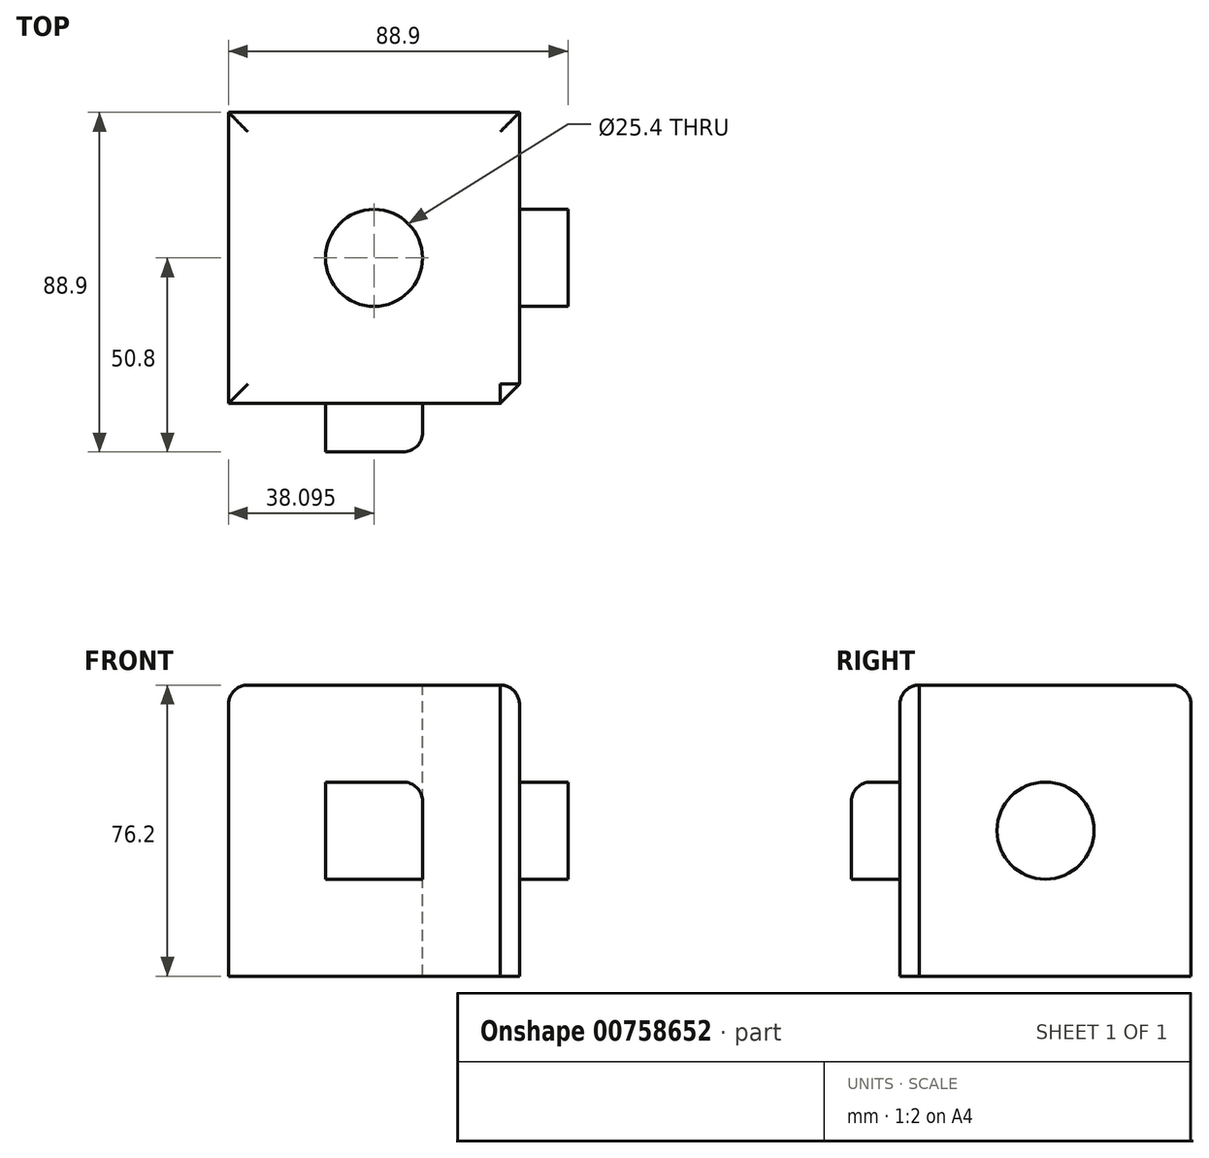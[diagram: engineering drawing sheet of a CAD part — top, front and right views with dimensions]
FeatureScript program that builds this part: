
annotation { "Feature Type Name" : "Feature", "Feature Type Description" : "" }
export const myFeature = defineFeature(function(context is Context, id is Id, definition is map)
    precondition{}
    {
        {
            var Q0;
            Q0=qCreatedBy(makeId("Front.planeOp"),FACE);
            var sketch = newSketch(context, id + "F0", { "sketchPlane" : qUnion([Q0])});
            skLineSegment(sketch, "E0.bottom", {"start": v(-8.54, 50.66) * mm, "end": v(67.66, 50.66) * mm});
            skLineSegment(sketch, "E0.top", {"start": v(-8.54, -25.54) * mm, "end": v(67.66, -25.54) * mm});
            skLineSegment(sketch, "E0.left", {"start": v(-8.54, 50.66) * mm, "end": v(-8.54, -25.54) * mm});
            skLineSegment(sketch, "E0.right", {"start": v(67.66, 50.66) * mm, "end": v(67.66, -25.54) * mm});
            skSolve(sketch);
        }
        {
            var Q0;
            Q0=makeQuery(id+"F0.imprint","IMPRINT",FACE,{"disambiguationData":[TD([[makeQuery(id+"F0.imprint","IMPRINT",EDGE,{"derivedFrom":sQuery(id+"F0.wireOp",EDGE,"E0.bottom")}),-1.0]])]});
            extrude(context, id + "F1", {"entities" : qUnion([Q0]), "depth" : 76.2 * mm, "offsetDistance" : 25.4 * mm});
        }
        {
            var Q0;
            Q0=makeQuery(id+"F1.opExtrude","CAP_FACE",FACE,{"disambiguationData":[OSD([sQuery(id+"F0.wireOp",EDGE,"E0.bottom"),sQuery(id+"F0.wireOp",EDGE,"E0.top"),sQuery(id+"F0.wireOp",EDGE,"E0.left"),sQuery(id+"F0.wireOp",EDGE,"E0.right")])],"isStart":false});
            var sketch = newSketch(context, id + "F2", { "sketchPlane" : qUnion([Q0])});
            skLineSegment(sketch, "E1.bottom", {"start": v(16.86, 25.26) * mm, "end": v(42.26, 25.26) * mm});
            skLineSegment(sketch, "E1.top", {"start": v(16.86, -0.14) * mm, "end": v(42.26, -0.14) * mm});
            skLineSegment(sketch, "E1.left", {"start": v(16.86, 25.26) * mm, "end": v(16.86, -0.14) * mm});
            skLineSegment(sketch, "E1.right", {"start": v(42.26, 25.26) * mm, "end": v(42.26, -0.14) * mm});
            skSolve(sketch);
        }
        {
            var Q0;
            Q0=makeQuery(id+"F2.imprint","IMPRINT",FACE,{"disambiguationData":[TD([[makeQuery(id+"F2.imprint","IMPRINT",EDGE,{"derivedFrom":sQuery(id+"F2.wireOp",EDGE,"E1.bottom")}),-1.0]])]});
            extrude(context, id + "F3", {"entities" : qUnion([Q0]), "operationType" : NewBodyOperationType.ADD, "depth" : 12.7 * mm, "offsetDistance" : 25.4 * mm});
        }
        {
            var Q0;
            Q0=makeQuery(id+"F1.opExtrude","SWEPT_FACE",FACE,{"disambiguationData":[OSD([sQuery(id+"F0.wireOp",EDGE,"E0.right")])]});
            var sketch = newSketch(context, id + "F4", { "sketchPlane" : qUnion([Q0])});
            skCircle(sketch, "E2", {"center": v(-38.1, 12.56) * mm, "radius": 12.7 * mm});
            skSolve(sketch);
        }
        {
            var Q0;
            Q0=makeQuery(id+"F4.imprint","IMPRINT",FACE,{"disambiguationData":[TD([[makeQuery(id+"F4.imprint","IMPRINT",EDGE,{"derivedFrom":sQuery(id+"F4.wireOp",EDGE,"E2")}),1.0]])]});
            extrude(context, id + "F5", {"entities" : qUnion([Q0]), "operationType" : NewBodyOperationType.ADD, "depth" : 12.7 * mm, "offsetDistance" : 25.4 * mm});
        }
        {
            var Q0;
            Q0=makeQuery(id+"F1.opExtrude","SWEPT_FACE",FACE,{"disambiguationData":[OSD([sQuery(id+"F0.wireOp",EDGE,"E0.bottom")])]});
            var sketch = newSketch(context, id + "F6", { "sketchPlane" : qUnion([Q0])});
            skPoint(sketch, "E3", {"position": v(29.56, -38.1) * mm});
            skSolve(sketch);
        }
        {
            var Q0;
            Q0=sQuery(id+"F6.wireOp",VERTEX,"E3");
            var Q1;
            Q1=makeQuery(id+"F1.opExtrude","SWEPT_BODY",BODY,{"disambiguationData":[OSD([sQuery(id+"F0.wireOp",EDGE,"E0.bottom"),sQuery(id+"F0.wireOp",EDGE,"E0.top"),sQuery(id+"F0.wireOp",EDGE,"E0.left"),sQuery(id+"F0.wireOp",EDGE,"E0.right")])]});
            hole(context, id + "F7", {"style" : HoleStyle.SIMPLE, "endStyle" : HoleEndStyle.THROUGH, "holeDiameter" : 25.4 * mm, "majorDiameter" : 6.35 * mm, "isTappedThrough" : true, "tappedDepth" : 12.7 * mm, "tapClearance" : 3, "locations" : qUnion([Q0]), "scope" : qUnion([Q1])});
        }
        {
            var Q0;
            Q0=makeQuery(id+"F1.opExtrude","CAP_EDGE",EDGE,{"disambiguationData":[OSD([sQuery(id+"F0.wireOp",EDGE,"E0.bottom")])],"isStart":false});
            var Q1;
            Q1=makeQuery(id+"F1.opExtrude","SWEPT_EDGE",EDGE,{"disambiguationData":[OSD([sQuery(id+"F0.wireOp",EDGE,"E0.bottom"),sQuery(id+"F0.wireOp",EDGE,"E0.left")])]});
            var Q2;
            Q2=makeQuery(id+"F1.opExtrude","SWEPT_EDGE",EDGE,{"disambiguationData":[OSD([sQuery(id+"F0.wireOp",EDGE,"E0.bottom"),sQuery(id+"F0.wireOp",EDGE,"E0.right")])]});
            var Q3;
            Q3=makeQuery(id+"F7.hole-0.boolean.opBoolean","COPY",EDGE,{"derivedFrom":makeQuery(id+"F7.hole-0.opRevolve","SWEPT_EDGE",EDGE,{"disambiguationData":[OSD([sQuery(id+"F7.hole-0.sketch.wireOp",EDGE,"core_line_2"),sQuery(id+"F7.hole-0.sketch.wireOp",EDGE,"core_line_3")])]})});
            var Q4;
            Q4=makeQuery(id+"F1.opExtrude","CAP_EDGE",EDGE,{"disambiguationData":[OSD([sQuery(id+"F0.wireOp",EDGE,"E0.bottom")])],"isStart":true});
            var Q5;
            Q5=makeQuery(id+"F3.opExtrude","CAP_EDGE",EDGE,{"disambiguationData":[OSD([sQuery(id+"F2.wireOp",EDGE,"E1.bottom")])],"isStart":false});
            var Q6;
            Q6=makeQuery(id+"F3.opExtrude","CAP_EDGE",EDGE,{"disambiguationData":[OSD([sQuery(id+"F2.wireOp",EDGE,"E1.right")])],"isStart":false});
            var Q7;
            Q7=makeQuery(id+"F3.opExtrude","SWEPT_EDGE",EDGE,{"disambiguationData":[OSD([sQuery(id+"F2.wireOp",EDGE,"E1.bottom"),sQuery(id+"F2.wireOp",EDGE,"E1.right")])]});
            fillet(context, id + "F8", {"entities" : qUnion([Q0, Q1, Q2, Q3, Q4, Q5, Q6, Q7]), "radius" : 5.08 * mm, "tangentPropagation" : true, "allowEdgeOverflow" : false});
        }
        {
            var Q0;
            Q0=makeQuery(id+"F1.opExtrude","CAP_EDGE",EDGE,{"disambiguationData":[OSD([sQuery(id+"F0.wireOp",EDGE,"E0.right")])],"isStart":false});
            chamfer(context, id + "F9", {"entities" : qUnion([Q0]), "width" : 5.08 * mm, "tangentPropagation" : true});
        }
    });
